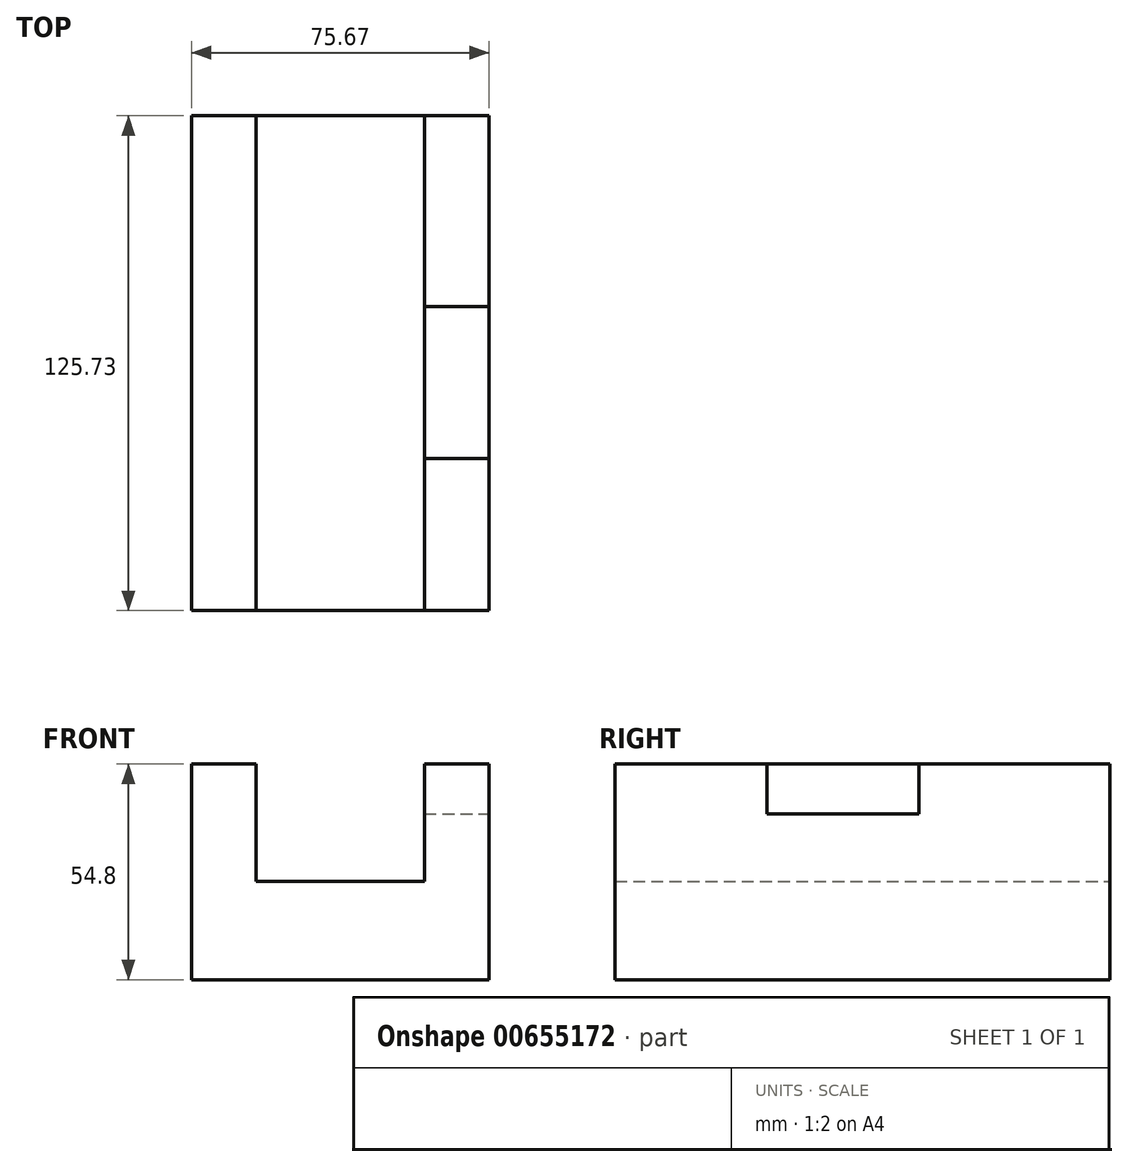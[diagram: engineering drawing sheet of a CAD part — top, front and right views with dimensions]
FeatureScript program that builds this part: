
annotation { "Feature Type Name" : "Feature", "Feature Type Description" : "" }
export const myFeature = defineFeature(function(context is Context, id is Id, definition is map)
    precondition{}
    {
        {
            var Q0;
            Q0=qCreatedBy(makeId("Front.planeOp"),FACE);
            var sketch = newSketch(context, id + "F0", { "sketchPlane" : qUnion([Q0])});
            skLineSegment(sketch, "E0.bottom", {"start": v(0, 0) * mm, "end": v(-75.67, 0) * mm});
            skLineSegment(sketch, "E0.top", {"start": v(0, 54.8) * mm, "end": v(-16.47, 54.8) * mm});
            skLineSegment(sketch, "E0.left", {"start": v(0, 0) * mm, "end": v(0, 54.8) * mm});
            skLineSegment(sketch, "E0.right", {"start": v(-75.67, 0) * mm, "end": v(-75.67, 54.8) * mm});
            skLineSegment(sketch, "E1.top", {"start": v(-59.2, 24.99) * mm, "end": v(-16.47, 24.99) * mm});
            skLineSegment(sketch, "E1.left", {"start": v(-59.2, 54.8) * mm, "end": v(-59.2, 24.99) * mm});
            skLineSegment(sketch, "E1.right", {"start": v(-16.47, 54.8) * mm, "end": v(-16.47, 24.99) * mm});
            skLineSegment(sketch, "E2.trimOffspring", {"start": v(-59.2, 54.8) * mm, "end": v(-75.67, 54.8) * mm});
            skSolve(sketch);
        }
        {
            var Q0;
            Q0 = qSketchRegion(id + "F0", true);
            extrude(context, id + "F1", {"entities" : qUnion([Q0]), "depth" : 125.73 * mm, "offsetDistance" : 25.4 * mm});
        }
        {
            var Q0;
            Q0=makeQuery(id+"F1.opExtrude","SWEPT_FACE",FACE,{"disambiguationData":[OSD([sQuery(id+"F0.wireOp",EDGE,"E0.top")])]});
            var sketch = newSketch(context, id + "F2", { "sketchPlane" : qUnion([Q0])});
            skLineSegment(sketch, "E3.bottom", {"start": v(-16.47, -48.5) * mm, "end": v(0, -48.5) * mm});
            skLineSegment(sketch, "E3.top", {"start": v(-16.47, -87.11) * mm, "end": v(0, -87.11) * mm});
            skLineSegment(sketch, "E3.left", {"start": v(-16.47, -48.5) * mm, "end": v(-16.47, -87.11) * mm});
            skLineSegment(sketch, "E3.right", {"start": v(0, -48.5) * mm, "end": v(0, -87.11) * mm});
            skSolve(sketch);
        }
        {
            var Q0;
            Q0 = qSketchRegion(id + "F2", true);
            extrude(context, id + "F3", {"entities" : qUnion([Q0]), "operationType" : NewBodyOperationType.REMOVE, "oppositeDirection" : true, "depth" : 12.7 * mm, "offsetDistance" : 25.4 * mm});
        }
    });
